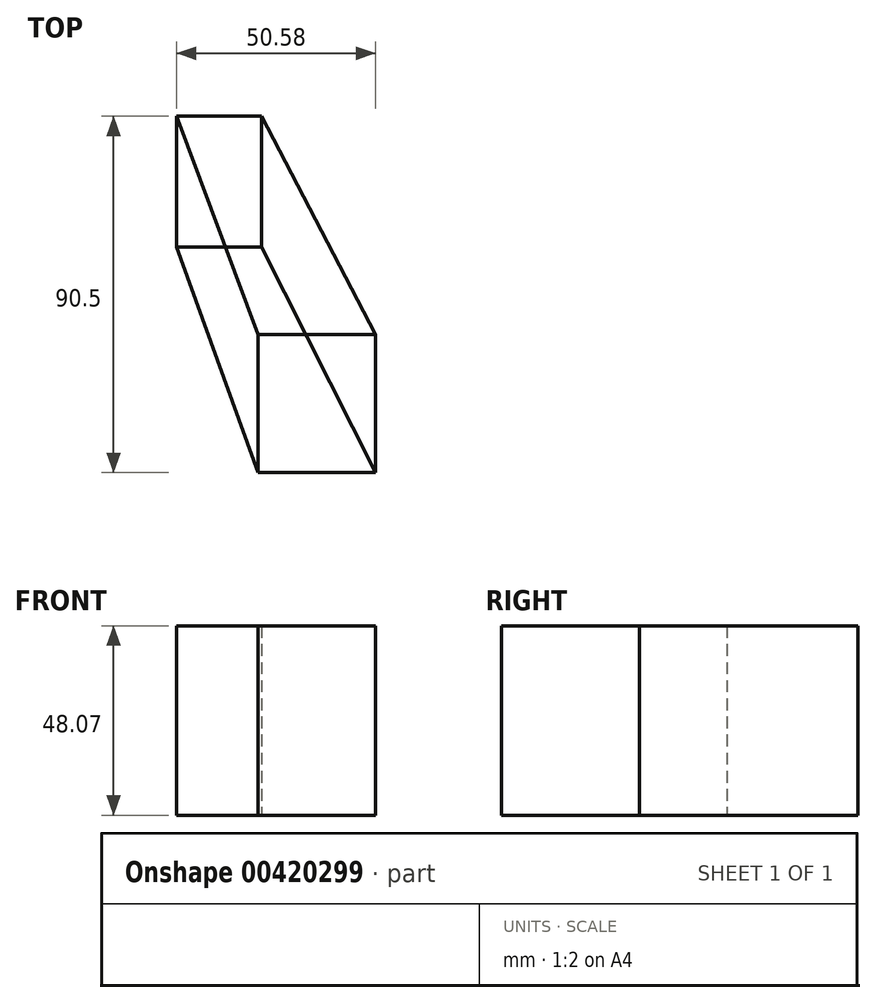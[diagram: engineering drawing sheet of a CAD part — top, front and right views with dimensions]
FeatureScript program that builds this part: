
annotation { "Feature Type Name" : "Feature", "Feature Type Description" : "" }
export const myFeature = defineFeature(function(context is Context, id is Id, definition is map)
    precondition{}
    {
        {
            var Q0;
            Q0=qCreatedBy(makeId("Top.planeOp"),FACE);
            var sketch = newSketch(context, id + "F0", { "sketchPlane" : qUnion([Q0])});
            skLineSegment(sketch, "E0.bottom", {"start": v(20.75, 0) * mm, "end": v(50.58, 0) * mm});
            skLineSegment(sketch, "E0.top", {"start": v(20.75, -35.08) * mm, "end": v(50.58, -35.08) * mm});
            skLineSegment(sketch, "E0.left", {"start": v(20.75, 0) * mm, "end": v(20.75, -35.08) * mm});
            skLineSegment(sketch, "E0.right", {"start": v(50.58, 0) * mm, "end": v(50.58, -35.08) * mm});
            skLineSegment(sketch, "E1.bottom", {"start": v(21.59, 22.2) * mm, "end": v(0, 22.2) * mm});
            skLineSegment(sketch, "E1.top", {"start": v(21.59, 55.42) * mm, "end": v(0, 55.42) * mm});
            skLineSegment(sketch, "E1.left", {"start": v(21.59, 22.2) * mm, "end": v(21.59, 55.42) * mm});
            skLineSegment(sketch, "E1.right", {"start": v(0, 22.2) * mm, "end": v(0, 55.42) * mm});
            skSolve(sketch);
        }
        {
            var Q0;
            Q0 = qSketchRegion(id + "F0", true);
            extrude(context, id + "F1", {"entities" : qUnion([Q0]), "depth" : 48.07 * mm});
        }
        {
            var Q0;
            Q0=makeQuery(id+"F1.opExtrude","SWEPT_FACE",FACE,{"disambiguationData":[OSD([sQuery(id+"F0.wireOp",EDGE,"E1.left")])]});
            var Q1;
            Q1=makeQuery(id+"F1.opExtrude","SWEPT_FACE",FACE,{"disambiguationData":[OSD([sQuery(id+"F0.wireOp",EDGE,"E0.right")])]});
            loft(context, id + "F2", {"sheetProfilesArray" : [{ "sheetProfileEntities" : qUnion([Q0]) }, { "sheetProfileEntities" : qUnion([Q1]) }]});
        }
        {
            var Q0;
            Q0=makeQuery(id+"F1.opExtrude","SWEPT_FACE",FACE,{"disambiguationData":[OSD([sQuery(id+"F0.wireOp",EDGE,"E1.right")])]});
            var Q1;
            Q1=makeQuery(id+"F1.opExtrude","SWEPT_FACE",FACE,{"disambiguationData":[OSD([sQuery(id+"F0.wireOp",EDGE,"E0.left")])]});
            loft(context, id + "F3", {"sheetProfilesArray" : [{ "sheetProfileEntities" : qUnion([Q0]) }, { "sheetProfileEntities" : qUnion([Q1]) }]});
        }
    });
